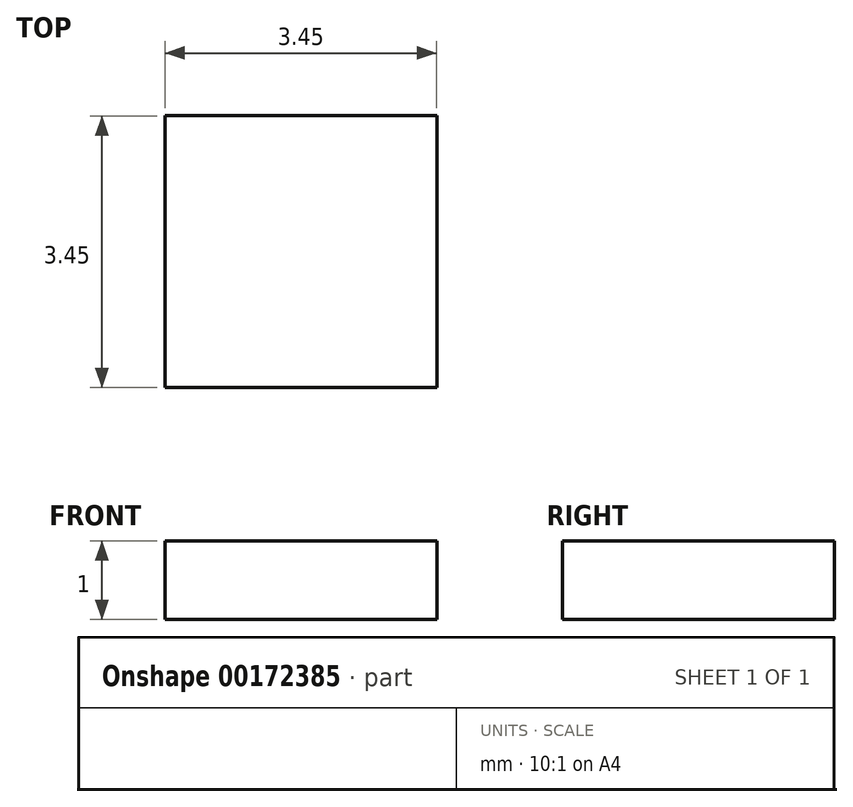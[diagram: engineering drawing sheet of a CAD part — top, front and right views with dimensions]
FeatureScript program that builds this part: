
annotation { "Feature Type Name" : "Feature", "Feature Type Description" : "" }
export const myFeature = defineFeature(function(context is Context, id is Id, definition is map)
    precondition{}
    {
        {
            var Q0;
            Q0=qCreatedBy(makeId("Top.planeOp"),FACE);
            var sketch = newSketch(context, id + "F0", { "sketchPlane" : qUnion([Q0])});
            skLineSegment(sketch, "E0.bottom", {"start": v(-34.85, -37.74) * mm, "end": v(-31.4, -37.74) * mm});
            skLineSegment(sketch, "E0.top", {"start": v(-34.85, -41.19) * mm, "end": v(-31.4, -41.19) * mm});
            skLineSegment(sketch, "E0.left", {"start": v(-34.85, -37.74) * mm, "end": v(-34.85, -41.19) * mm});
            skLineSegment(sketch, "E0.right", {"start": v(-31.4, -37.74) * mm, "end": v(-31.4, -41.19) * mm});
            skSolve(sketch);
        }
        {
            var Q0;
            Q0 = qSketchRegion(id + "F0", true);
            extrude(context, id + "F1", {"entities" : qUnion([Q0]), "depth" : 1 * mm});
        }
    });
